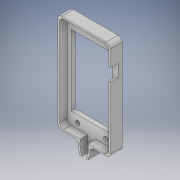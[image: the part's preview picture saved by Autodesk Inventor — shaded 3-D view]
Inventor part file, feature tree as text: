
AUTODESK INVENTOR PART (.ipt)
format: ipt  version: 2017 (Build 210142000, 142)  size: 233,472 bytes
history: native  units: in
note: dims shown in document units (in); Inventor stores cm internally (conversion verified against a paired STEP export)
features: sketch x7, extrude x6, fillet x5, hole x1, plane x1, mirror x1
ambient origin geometry x8: Origin, YZ Plane, XZ Plane, XY Plane, X Axis, Y Axis, Z Axis, Center Point
bodies: Solid1 (feature_tree)
feature tree (21):
  extrude  "Extrusion1"  Depth=6.0in
  extrude  "Extrusion2"  Depth=0.35in
  extrude  "Extrusion3"  Depth=4.3in
  fillet  "Fillet1"  Radius=0.25in
  fillet  "Fillet2"  Radius=0.1in
  fillet  "Fillet3"  Radius=0.1in
  extrude  "Extrusion4"  Depth=5.8in
  fillet  "Fillet4"  Radius=0.46in
  fillet  "Fillet5"  Radius=1.35in
  extrude  "Extrusion5"  Depth=1.225in
  hole  "Hole1"  [1 undecoded]
  extrude  "Extrusion6"  Depth=0.25in
  plane  "Work Plane1"
  mirror  "Mirror1"
  sketch  "Sketch1"  dims[d0=3.2in d1=6.0in]
  sketch  "Sketch2"  dims[d2=0.85in d3=0.35in]
  sketch  "Sketch3"  dims[d4=2.5in d5=4.3in d6=0.25in d7=0.0in d8=0.1in d9=0.1in]
  sketch  "Sketch4"  dims[d10=3.0in d11=5.8in d12=0.46in d13=0.0in d14=1.35in]
  sketch  "Sketch5"  dims[d15=0.5in d16=1.225in]
  sketch  "Sketch6"  dims[d17=0.75in d18=0.46in d19=0.0in]
  sketch  "Sketch7"  dims[d20=0.25in d21=0.25in d22=0.25in d24=0.75in d25=0.125in d26=0.125in d27=1.5in d28=1.5in d29=0.1in d30=0.1in d31=1.5in d32=1.5in d33=0.125in d34=0.71in d35=0.0in d36=0.25in d37=0.25in d38=0.25in d39=0.0in d40=0.425in d41=0.425in d42=0.75in d43=0.75in d44=0.145in d45=0.75in d46=0.375in d47=0.25in d48=0.5635in d49=1.0in d50=0.8108in d51=0.275in d52=0.275in d53=0.1in d54=0.0in]
note: 1 required parameter value undecoded (feature->parameter linkage not recoverable at this tier; creation-order binding heuristic only, values carry confidence <= 0.55)
